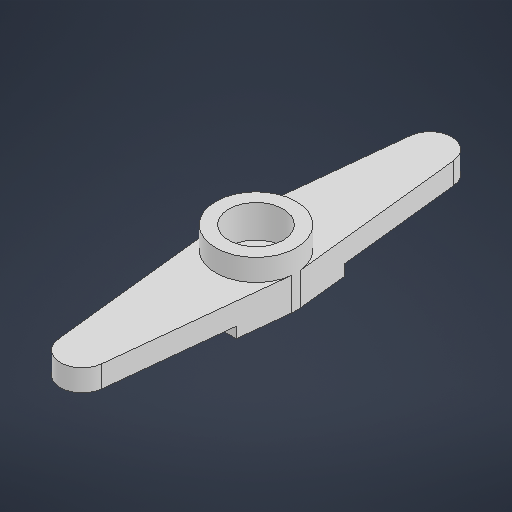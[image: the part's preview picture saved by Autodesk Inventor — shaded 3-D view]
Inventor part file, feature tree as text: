
AUTODESK INVENTOR PART (.ipt)
format: ipt  version: 2025.1 (Build 291241000, 241)  size: 231,424 bytes
history: native  units: mm
features: extrude x4, sketch x4, projected_geometry x2, hole x1
ambient origin geometry x8: Origin, YZ Plane, XZ Plane, XY Plane, X Axis, Y Axis, Z Axis, Center Point
bodies: Solid1 (feature_tree)
feature tree (11):
  extrude  "Extrusion1"  Depth=7.4mm
  sketch  "Sketch2"  dims[d2=18.0mm d3=2.0mm d4=0.0mm]
  extrude  "Extrusion2"  Depth=2.0mm TaperAngle=0.0deg
  extrude  "Extrusion3"  Depth=2.0mm TaperAngle=0.0deg
  extrude  "Extrusion4"  Depth=10.0mm
  hole  "Hole1"  [1 undecoded]
  sketch  "Sketch1"  dims[d0=4.0mm d1=7.4mm]
  projected_geometry  "Projected Loop1"
  sketch  "Sketch3"  dims[d5=1.2mm d6=2.0mm d7=0.0mm]
  projected_geometry  "Projected Loop2"
  sketch  "Sketch4"  dims[d8=1.0mm d9=0.0mm d10=10.0mm d11=1.0mm d12=0.0mm d13=2.3mm d14=6.0mm d15=4.0mm d16=2.0mm d17=90.0deg d18=8.0mm d19=20.594885mm]
note: 1 required parameter value undecoded (feature->parameter linkage not recoverable at this tier; creation-order binding heuristic only, values carry confidence <= 0.55)
